# Revit family: Echo Eliminator - Ceiling and Wall Panels
name_source: partatom
category: Generic Models
revit_build: Autodesk Revit 2016 (Build: 20150220_1215(x64)
units: mm (PartAtom-declared; Revit-internal decimal feet)

## family parameters
Always vertical = No
Can host rebar = No
Cut with Voids When Loaded = No
Part Type = Normal
Room Calculation Point = No
Round Connector Dimension = Use Diameter
Shared = No
Work Plane-Based = Yes

## types (46) — shared parameters
A = 0' - 0"
Default Elevation = 4' - 0"
Manufacturer = Acoustical Surfaces, Inc.
Material = PolyMax
URL = https://www.acousticalsurfaces.com

## per-type parameters (varying)
| type | Finish | Length | T | Thickness Options | Width | ‍      1. Thickness 1" | ‍      2. Thickness 2" |
| 1 INCH THICK - 24x48 - Grey | Echo Eliminator - Grey | 4' - 0" | 0' - 1" | 1 | 2' - 0" | Yes | No |
| 1 INCH THICK - 48X96 - Black | Echo Eliminator - Black | 8' - 0" | 0' - 1" | 1 | 4' - 0" | Yes | No |
| 1 INCH THICK - 48X96 Beige | Echo Eliminator - Beige | 8' - 0" | 0' - 1" | 1 | 4' - 0" | Yes | No |
| 1 INCH THICK - 48X96 - White | Echo Eliminator - White | 8' - 0" | 0' - 1" | 1 | 4' - 0" | Yes | No |
| 2 INCH THICK - 48X96 - Black | Echo Eliminator - Black | 8' - 0" | 0' - 2" | 2 | 4' - 0" | No | Yes |
| 2 INCH THICK - 48X96 - Beige | Echo Eliminator - Beige | 8' - 0" | 0' - 2" | 2 | 4' - 0" | No | Yes |
| 2 INCH THICK - 48X96 - White | Echo Eliminator - White | 8' - 0" | 0' - 2" | 2 | 4' - 0" | No | Yes |
| 2 INCH THICK - 24x48 - Printed Graphics | Echo Eliminator - Marble Blue | 4' - 0" | 0' - 2" | 2 | 2' - 0" | No | Yes |
| 2 INCH THICK - 24x48 - Charcoal | Echo Eliminator - Charcoal | 4' - 0" | 0' - 2" | 2 | 2' - 0" | No | Yes |
| 2 INCH THICK - 24x48 - Black | Echo Eliminator - Black | 4' - 0" | 0' - 2" | 2 | 2' - 0" | No | Yes |
| 2 INCH THICK - 24x48 - White | Echo Eliminator - White | 4' - 0" | 0' - 2" | 2 | 2' - 0" | No | Yes |
| 1 INCH THICK - 24x48 - Charcoal | Echo Eliminator - Charcoal | 4' - 0" | 0' - 1" | 1 | 2' - 0" | Yes | No |
| 1 INCH THICK - 24x48 - Black | Echo Eliminator - Black | 4' - 0" | 0' - 1" | 1 | 2' - 0" | Yes | No |
| 1 INCH THICK - 24x48 - Beige | Echo Eliminator - Beige | 4' - 0" | 0' - 1" | 1 | 2' - 0" | Yes | No |
| 1 INCH THICK - 24x48 - White | Echo Eliminator - White | 4' - 0" | 0' - 1" | 1 | 2' - 0" | Yes | No |
| 2 INCH THICK - 24x48 - Beige | Echo Eliminator - Beige | 4' - 0" | 0' - 2" | 2 | 2' - 0" | No | Yes |
| 1 INCH THICK - 24x48 - Marble Blue | Echo Eliminator - Marble Blue | 4' - 0" | 0' - 1" | 1 | 2' - 0" | Yes | No |
| 2 INCH THICK - 48x48 - Black | Echo Eliminator - Black | 4' - 0" | 0' - 2" | 2 | 4' - 0" | No | Yes |
| 2 INCH THICK - 48x48 - Charcoal | Echo Eliminator - Charcoal | 4' - 0" | 0' - 2" | 2 | 4' - 0" | No | Yes |
| 2 INCH THICK - 48x48 - Gray | Echo Eliminator - Grey | 4' - 0" | 0' - 2" | 2 | 4' - 0" | No | Yes |
| 2 INCH THICK - 48x48 - Printed Graphics | Echo Eliminator - Marble Blue | 4' - 0" | 0' - 2" | 2 | 4' - 0" | No | Yes |
| 2 INCH THICK - 48x48 - Beige | Echo Eliminator - Beige | 4' - 0" | 0' - 2" | 2 | 4' - 0" | No | Yes |
| 2 INCH THICK - 48x48 - White | Echo Eliminator - White | 4' - 0" | 0' - 2" | 2 | 4' - 0" | No | Yes |
| 1 INCH THICK - 48x48 - Black | Echo Eliminator - Black | 4' - 0" | 0' - 1" | 1 | 4' - 0" | Yes | No |
| 1 INCH THICK - 48x48 - Charcoal | Echo Eliminator - Charcoal | 4' - 0" | 0' - 1" | 1 | 4' - 0" | Yes | No |
| 1 INCH THICK - 48x48 - Grey | Echo Eliminator - Grey | 4' - 0" | 0' - 1" | 1 | 4' - 0" | Yes | No |
| 1 INCH THICK - 48x48 - Marble Blue | Echo Eliminator - Marble Blue | 4' - 0" | 0' - 1" | 1 | 4' - 0" | Yes | No |
| 1 INCH THICK - 48x48 - Beige | Echo Eliminator - Beige | 4' - 0" | 0' - 1" | 1 | 4' - 0" | Yes | No |
| 1 INCH THICK - 48x48 - White | Echo Eliminator - White | 4' - 0" | 0' - 1" | 1 | 4' - 0" | Yes | No |
| 2 INCH THICK - 24x24 - Black | Echo Eliminator - Black | 2' - 0" | 0' - 2" | 2 | 2' - 0" | No | Yes |
| 1 INCH THICK - 24x24 - Black | Echo Eliminator - Black | 2' - 0" | 0' - 1" | 1 | 2' - 0" | Yes | No |
| 2 INCH THICK - 24x24 - Charcoal | Echo Eliminator - Charcoal | 2' - 0" | 0' - 2" | 2 | 2' - 0" | No | Yes |
| 1 INCH THICK - 24x24 - Charcoal | Echo Eliminator - Charcoal | 2' - 0" | 0' - 1" | 1 | 2' - 0" | Yes | No |
| 2 INCH THICK - 24x24 - Gray | Echo Eliminator - Grey | 2' - 0" | 0' - 2" | 2 | 2' - 0" | No | Yes |
| 1 INCH THICK - 24x24 - Grey | Echo Eliminator - Grey | 2' - 0" | 0' - 1" | 1 | 2' - 0" | Yes | No |
| 2 INCH THICK - 24x24 - Printed Graphics | Echo Eliminator - Marble Blue | 2' - 0" | 0' - 2" | 2 | 2' - 0" | No | Yes |
| 1 INCH THICK - 24x24 - Marble Blue | Echo Eliminator - Marble Blue | 2' - 0" | 0' - 1" | 1 | 2' - 0" | Yes | No |
| 2 INCH THICK - 24x24 - Beige | Echo Eliminator - Beige | 2' - 0" | 0' - 2" | 2 | 2' - 0" | No | Yes |
| 1 INCH THICK - 24x24 - Beige | Echo Eliminator - Beige | 2' - 0" | 0' - 1" | 1 | 2' - 0" | Yes | No |
| 2 INCH THICK - 24x24 - White | Echo Eliminator - White | 2' - 0" | 0' - 2" | 2 | 2' - 0" | No | Yes |
| 1 INCH THICK - 24x24 - White | Echo Eliminator - White | 2' - 0" | 0' - 1" | 1 | 2' - 0" | Yes | No |
| 2 INCH THICK - 24x48 - Gray | Echo Eliminator - Grey | 4' - 0" | 0' - 2" | 2 | 2' - 0" | No | Yes |
| 1 INCH THICK - 48X96 - Marble Blue | Echo Eliminator - Marble Blue | 8' - 0" | 0' - 1" | 1 | 4' - 0" | Yes | No |
| 1 INCH THICK - 48X96 - Charcoal | Echo Eliminator - Charcoal | 8' - 0" | 0' - 1" | 1 | 4' - 0" | Yes | No |
| 2 INCH THICK - 48X96 - Marble Blue | Echo Eliminator - Marble Blue | 8' - 0" | 0' - 2" | 2 | 4' - 0" | No | Yes |
| 2 INCH THICK - 48X96 - Charcoal | Echo Eliminator - Charcoal | 8' - 0" | 0' - 2" | 2 | 4' - 0" | No | Yes |

## geometry (parser evidence)
native form markers: Sweep x8
no freeform markers — native parametric forms only
